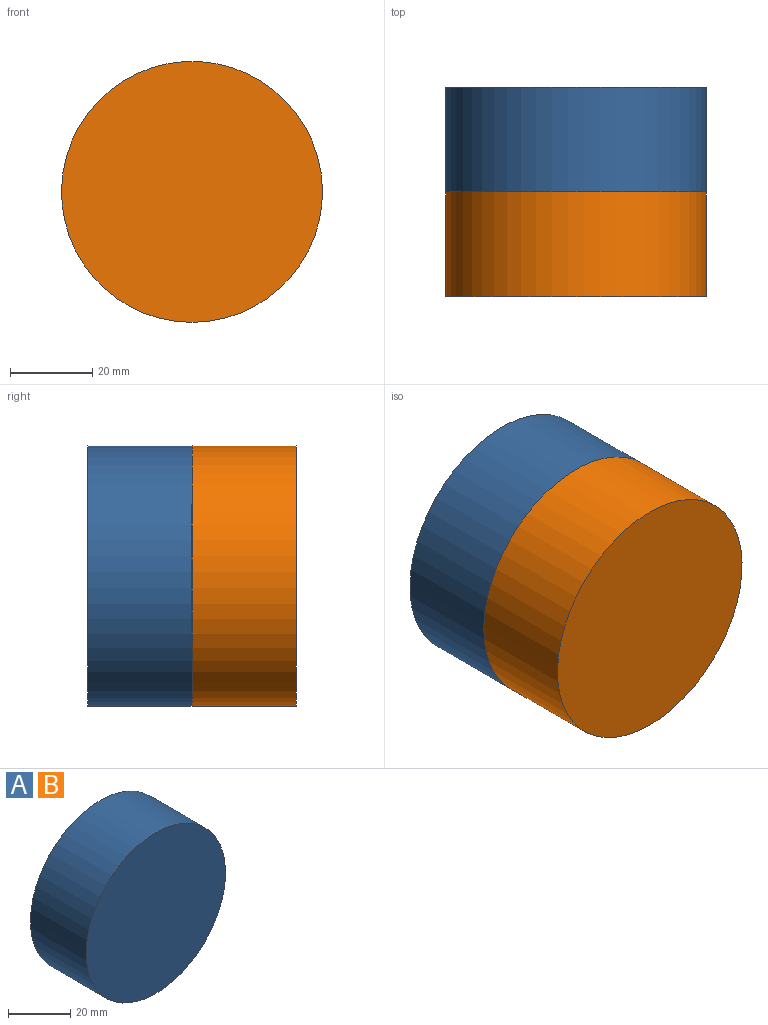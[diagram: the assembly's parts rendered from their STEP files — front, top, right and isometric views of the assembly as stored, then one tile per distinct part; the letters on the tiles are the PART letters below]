
ASSEMBLY  parts=2 mates=1
PART A: 3 faces, bbox 63.5x25.4x63.5 mm
  f0: cylinder r=31.75mm len=63.5mm, axis (0,1,0), area 5067.1mm2, adj f1,f2
  f1: plane 63.5x63.5mm, normal (0,-1,0), area 3166.9mm2, adj f0
  f2: plane 63.5x63.5mm, normal (0,1,0), area 3166.9mm2, adj f0
PART B: same geometry as A
PLACE A t=(19.37,25.71,2.74)mm
PLACE B t=(19.37,0.31,2.74)mm
MATE fastened B.f0 <-> A.f0  axis (0,1,0) through (19.37,0.31,2.74)mm
